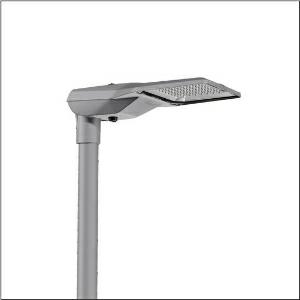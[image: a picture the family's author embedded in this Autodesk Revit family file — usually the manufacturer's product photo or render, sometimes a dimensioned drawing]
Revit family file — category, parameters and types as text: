
# Revit family: streetlight_sl_21_iq_midi___st1_0ab_5xe3m31y08nb_fb51
name_source: partatom
category: Lighting Fixtures
units: mm (PartAtom-declared; Revit-internal decimal feet)

## family parameters
Cut with Voids When Loaded = No
Host = Face
Light Source = No
Part Type = Normal
Room Calculation Point = No
Round Connector Dimension = Use Diameter
Shared = No

## types (1)
- --- (1 x LED, 18970 lm, 136.6 W, 3000K)
    Apparent Load = 137 VA
    CIE Flux Codes = 40 74 97 100 100
    Color Rendering = 70
    Color Temperature = 3000K
    Default Elevation = 1800 mm
    Description = Streetlight SL 21 iQ midi, mast luminaire, primary light control with lens, of PMMA, primary optical cover: cover, of toughened safety glass, transparent, light distribution: ST1.0aB, light emission: direct distribution, primary light characteristic: asymmetric, installation type: post-top, side-entry, LED, High Power LED, rated luminous flux: 18.970lm, luminous efficacy: 139lm/W, light colour: 730, colour temperature: 3000K, control gear: iQ-Street Remote, D4i with power reduction, control: pre-setting: logarithmic dimming characteristic, Street-Remote, Auto-Match, Temp-Guard, Lumen-Switch, Night-Set, Smart-Wire, Light-Fading, Desk-Remote (wireless, voltage-free reading and setting of iQ features in the workshop via application-optimized NFC function/RFID function), optimised constant luminous flux control (CLO 2.0), mains connection: 230..240V, AC, 50/60Hz, start of lifetime: 137W, end of service life: 144W, reduction: 61W, luminaire housing, of diecast aluminium, powder-coated, SITECO metallic grey (DB 702S), corrosivity category C5 high according to DIN EN ISO 12944, please order mast flange separately, inclination adjustable: 0°, 5°, 10°, 15°, sealing non-destructively replaceable, multi-level sealing system, length: 644mm, width: 335mm, height: 110mm, mast flange for spigot size: 42mm (side-entry): 5XC10008XM4, 60/48mm (side-entry/post-top): 5XC10108XM2, 76/60mm (side-entry/post-top): 5XC10108XM1, mounting height: 4..8m, Smart Interface below and above, protection rating (complete): IP66, insulation class (complete): insulation class II (safety insulation), certification: CE, ENEC, ENEC+, VDE, impact resistance: IK10, permissible operating ambient temperature for outdoor applications: -40..+50°C, standard-compliant lighting for roads and squares, packaging unit: 1 piece

Light Distribution: ST1.0aB
    Height = 111 mm
    Lamp = 1 x LED
    Lamp Light Flux = 18970 lm
    Lamp Power = 136.6 W
    Lamp count = 1
    Length = 644 mm
    Luminous efficacy = 139 lm/W
    Manufacturer = Siteco
    ModVariant = No
    Model = 5XE3M31Y08NB
    Number of Poles = 1
    OnlyDefault = Yes
    Power Factor = 1
    Product Name = Streetlight SL 21 iQ midi | ST1.0aB
    Product group = mast luminaire | pylon top
    ProductGroupID = 6100
    Protection Class = Protection class II
    Protection Degree = IP 66
    RLX_Detail_Level = 1
    RLX_Emergency_Light_Flux = 0 lm
    RLX_Emergency_Type = 0
    RLX_Emergency_Type_DB = No
    RlxData = <blob elided: 91085 chars, md5=6ad7e1a0>
    Socket = socket
    Standby Power = 0 W
    System Light Flux = 18970 lm
    System Power = 137 W
    Type Comments = factory setting: luminous flux: 100 % | dim-lin: 254 | 733 mA
    Type Image = l_1004304.jpg
    URL = http://relux.com
    VarID = @adj_112049
    Voltage = 0 V
    Weight = 0.00 kg
    Width = 336 mm

## geometry (parser evidence)
native form markers: Blend x4, Sweep x10
no freeform markers — native parametric forms only
